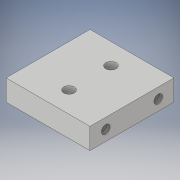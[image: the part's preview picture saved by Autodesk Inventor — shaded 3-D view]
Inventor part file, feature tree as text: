
AUTODESK INVENTOR PART (.ipt)
format: ipt  version: 2017 (Build 210142000, 142)  size: 121,856 bytes
history: native  units: in
note: dims shown in document units (in); Inventor stores cm internally (conversion verified against a paired STEP export)
features: sketch x3, extrude x2, hole x1
ambient origin geometry x8: Origin, YZ Plane, XZ Plane, XY Plane, X Axis, Y Axis, Z Axis, Center Point
bodies: Solid1 (feature_tree)
feature tree (6):
  extrude  "Extrusion1"  Depth=0.25in
  extrude  "Extrusion2"  Depth=0.25in
  hole  "Hole1"  [1 undecoded]
  sketch  "Sketch1"  dims[d0=1.0in d1=0.25in]
  sketch  "Sketch2"  dims[d2=1.0in d3=0.0in d4=0.25in]
  sketch  "Sketch3"  dims[d5=0.25in d6=0.125in d7=0.125in d8=1.0in d9=0.0in d10=0.104in d11=0.275in d12=0.375in d13=0.25in d14=0.5635in d15=0.325in d16=0.8108in]
note: 1 required parameter value undecoded (feature->parameter linkage not recoverable at this tier; creation-order binding heuristic only, values carry confidence <= 0.55)
